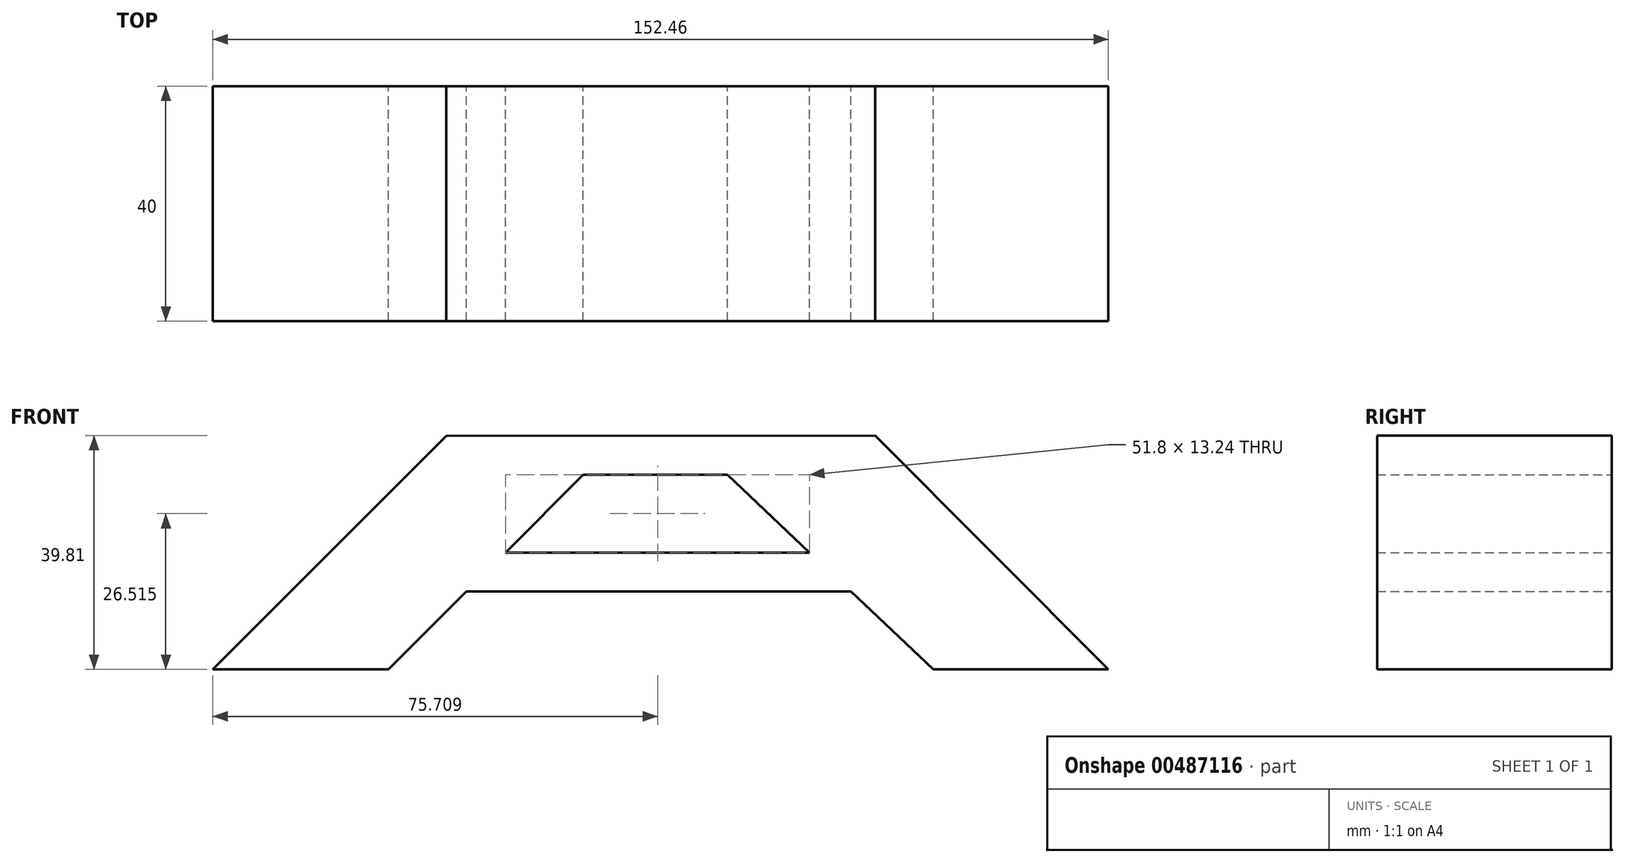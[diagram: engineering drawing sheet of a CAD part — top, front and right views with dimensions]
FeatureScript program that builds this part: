
annotation { "Feature Type Name" : "Feature", "Feature Type Description" : "" }
export const myFeature = defineFeature(function(context is Context, id is Id, definition is map)
    precondition{}
    {
        {
            var Q0;
            Q0=qCreatedBy(makeId("Front.planeOp"),FACE);
            var sketch = newSketch(context, id + "F0", { "sketchPlane" : qUnion([Q0])});
            skLineSegment(sketch, "E0", {"start": v(76.08, -74.04) * mm, "end": v(36.37, -34.23) * mm});
            skLineSegment(sketch, "E1", {"start": v(-76.38, -74.04) * mm, "end": v(-36.62, -34.29) * mm});
            skLineSegment(sketch, "E2", {"start": v(-36.62, -34.29) * mm, "end": v(36.37, -34.23) * mm});
            skLineSegment(sketch, "E3", {"start": v(76.08, -74.04) * mm, "end": v(46.28, -74.04) * mm});
            skLineSegment(sketch, "E4", {"start": v(-76.38, -74.04) * mm, "end": v(-46.47, -74.04) * mm});
            skLineSegment(sketch, "E5", {"start": v(-13.33, -40.9) * mm, "end": v(11.23, -40.9) * mm});
            skLineSegment(sketch, "E6", {"start": v(-33.22, -60.8) * mm, "end": v(32.26, -60.8) * mm});
            skLineSegment(sketch, "E7", {"start": v(25.23, -54.14) * mm, "end": v(-26.57, -54.14) * mm});
            skLineSegment(sketch, "E8", {"start": v(-46.47, -74.04) * mm, "end": v(-33.22, -60.8) * mm});
            skLineSegment(sketch, "E9", {"start": v(-26.57, -54.14) * mm, "end": v(-13.33, -40.9) * mm});
            skLineSegment(sketch, "E10", {"start": v(11.23, -40.9) * mm, "end": v(25.23, -54.14) * mm});
            skLineSegment(sketch, "E11", {"start": v(32.26, -60.8) * mm, "end": v(46.28, -74.04) * mm});
            skSolve(sketch);
        }
        {
            var Q0;
            Q0 = qSketchRegion(id + "F0", true);
            extrude(context, id + "F1", {"entities" : qUnion([Q0]), "depth" : 40 * mm});
        }
    });
